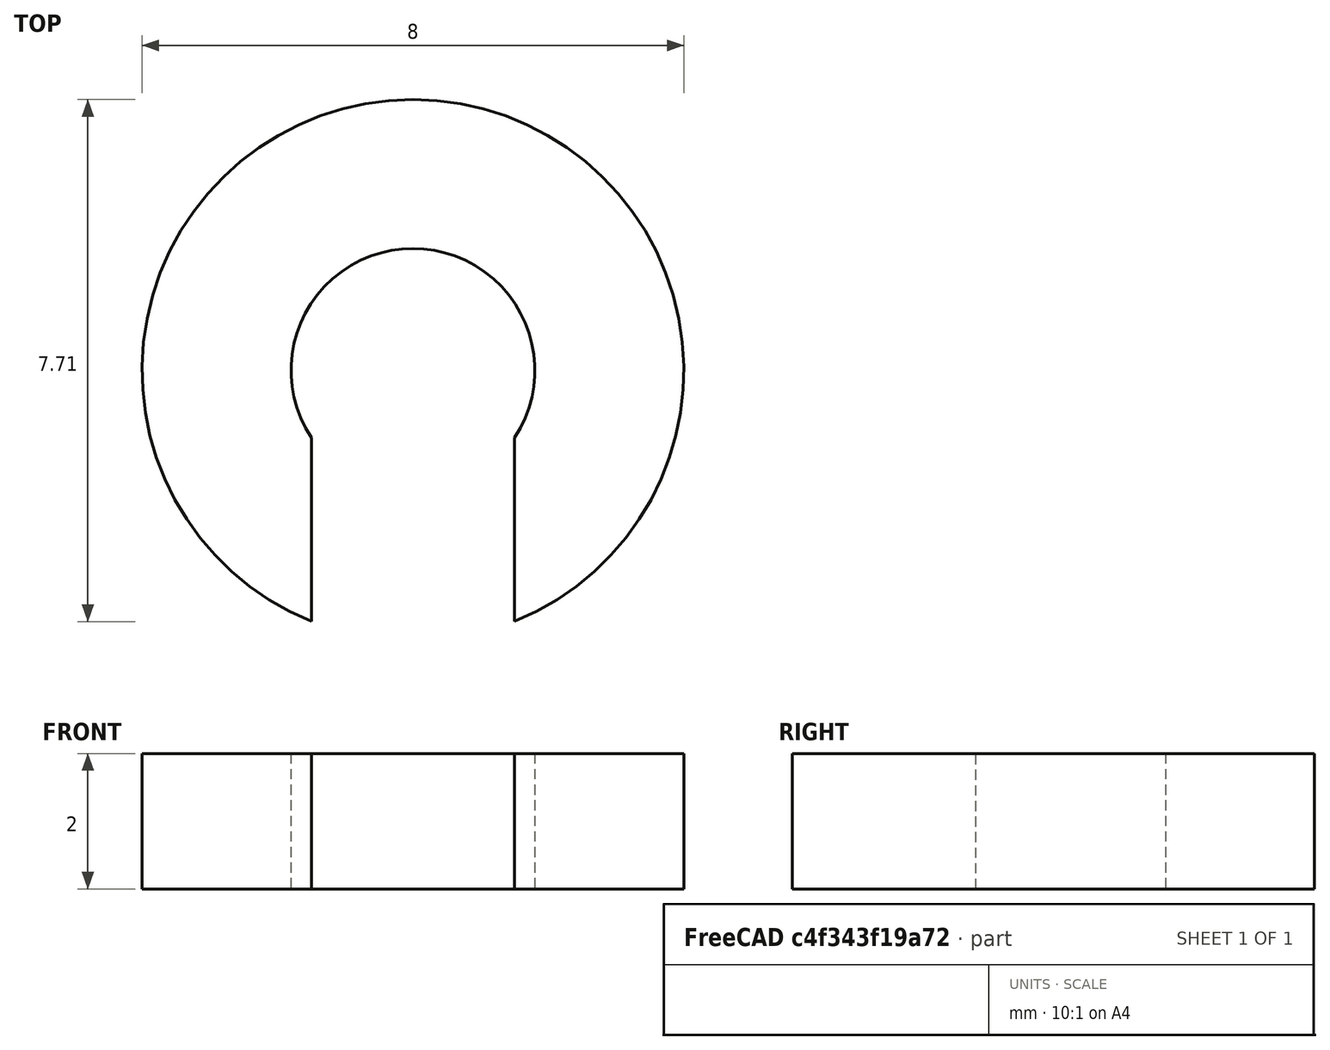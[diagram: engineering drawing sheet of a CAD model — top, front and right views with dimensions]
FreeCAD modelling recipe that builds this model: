
FCSTD DOCUMENT  (FreeCAD 0.17R13541 (Git))
Label: buteeSoupape2
License: All rights reserved
LicenseURL: http://en.wikipedia.org/wiki/All_rights_reserved
objects: Sketcher::SketchObject×1, PartDesign::Pad×1, PartDesign::Body×1
note: 4 computed .brp shape members not serialized (recipe doc carries the construction recipe); baked Part::Feature solids carry a one-line shape summary decoded from their .brp

FEATURE [Sketcher::SketchObject] Sketch
  MapMode = 5
  Support = -> [XY_Plane]
  sketch-geometry (4):
    g0: ArcOfCircle CenterX=0 CenterY=0 CenterZ=0 NormalX=0 NormalY=0 NormalZ=1 AngleXU=0 Radius=1.8 StartAngle=5.6975 EndAngle=10.0105
    g1: LineSegment StartX=-1.5 StartY=-0.994987 StartZ=0 EndX=-1.5 EndY=-3.7081 EndZ=0
    g2: LineSegment StartX=1.5 StartY=-0.994987 StartZ=0 EndX=1.5 EndY=-3.7081 EndZ=0
    g3: ArcOfCircle CenterX=0 CenterY=0 CenterZ=0 NormalX=0 NormalY=0 NormalZ=1 AngleXU=0 Radius=4 StartAngle=5.09679 EndAngle=10.6112
  constraints (10):
    c: Coincident(g0,g-1)
    c: Radius(g0) = 1.8
    c: Vertical(g1)
    c: Vertical(g2)
    c: Coincident(g0,g2)
    c: Coincident(g0,g1)
    c: Coincident(g3,g-1)
    c: Radius(g3) = 4
    c: PointOnObject(g3,g2)
    c: PointOnObject(g3,g1)
FEATURE [PartDesign::Pad] Pad
  Length = 2
  Length2 = 100
  Profile = -> Sketch
  Type = 0
FEATURE [PartDesign::Body] Body
  Group = -> [Sketch,Pad]
  Origin = -> Origin
  Tip = -> Pad
